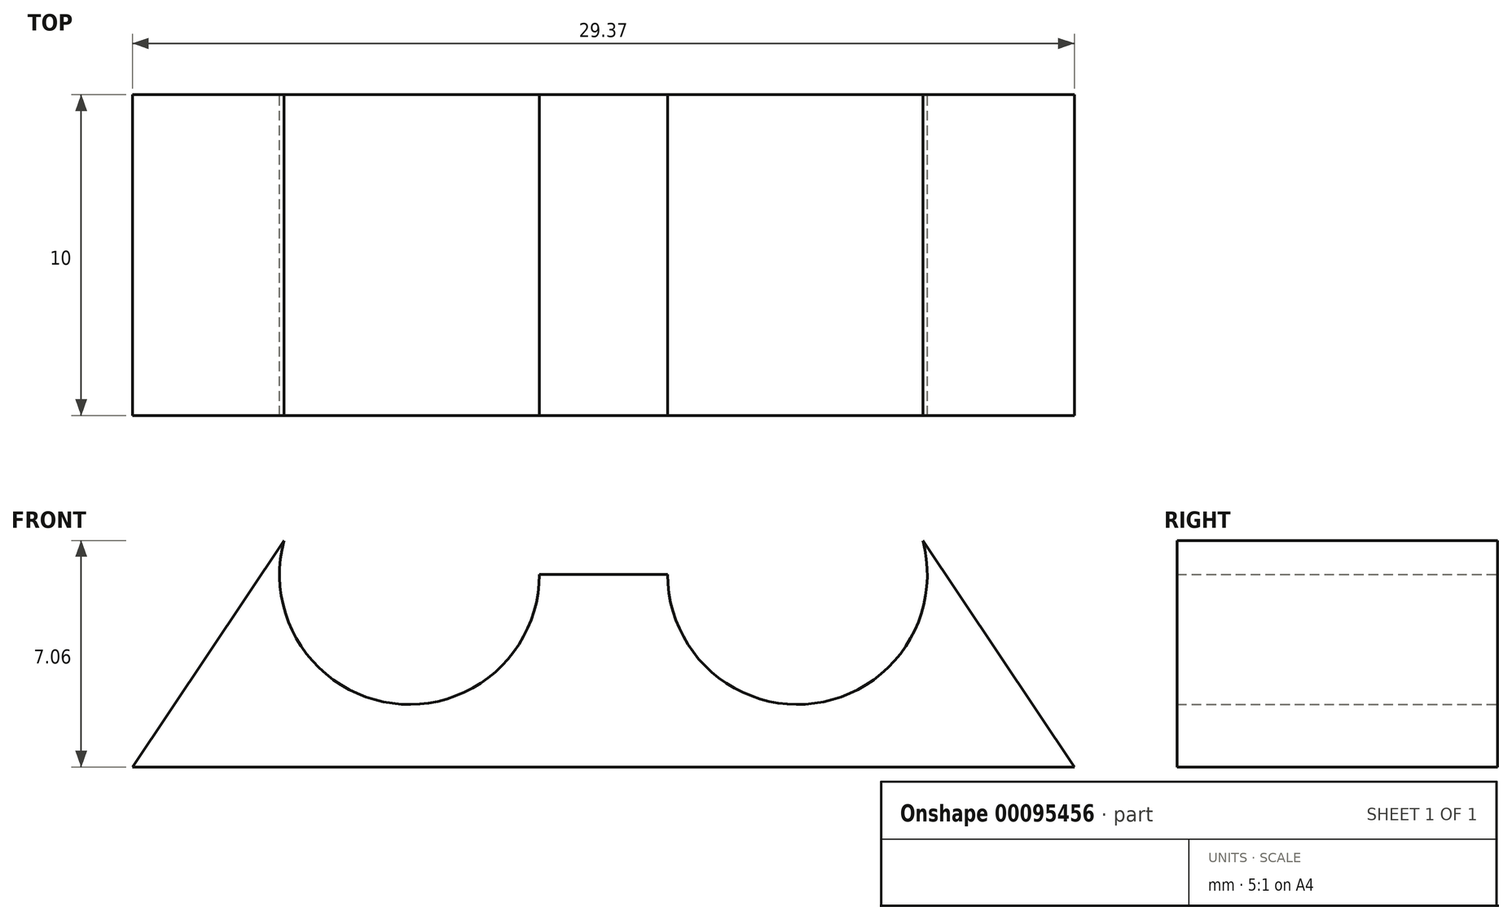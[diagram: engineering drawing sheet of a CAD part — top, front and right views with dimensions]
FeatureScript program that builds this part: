
annotation { "Feature Type Name" : "Feature", "Feature Type Description" : "" }
export const myFeature = defineFeature(function(context is Context, id is Id, definition is map)
    precondition{}
    {
        {
            var Q0;
            Q0=qCreatedBy(makeId("Front.planeOp"),FACE);
            var sketch = newSketch(context, id + "F0", { "sketchPlane" : qUnion([Q0])});
            skArc(sketch, "E0", {"start": v(-27.77, 1.06) * mm, "mid": v(-24.4, -4.01) * mm, "end": v(-19.81, 0) * mm});
            skLineSegment(sketch, "E1", {"start": v(0, 0) * mm, "end": v(-102.74, 0) * mm, "construction": true});
            skLineSegment(sketch, "E2", {"start": v(-27.77, 1.06) * mm, "end": v(-32.5, -6) * mm});
            skLineSegment(sketch, "E3", {"start": v(-32.5, -6) * mm, "end": v(-17.81, -6) * mm});
            skLineSegment(sketch, "E4", {"start": v(-19.81, 0) * mm, "end": v(-17.81, 0) * mm});
            skLineSegment(sketch, "E5", {"start": v(-17.81, 0) * mm, "end": v(-17.81, -6) * mm});
            skLineSegment(sketch, "E6.MirrorCS", {"start": v(-15.81, 0) * mm, "end": v(-17.81, 0) * mm});
            skArc(sketch, "E7.MirrorCS", {"start": v(-7.85, 1.06) * mm, "mid": v(-11.23, -4.01) * mm, "end": v(-15.81, 0) * mm});
            skLineSegment(sketch, "E8.MirrorCS", {"start": v(-7.85, 1.06) * mm, "end": v(-3.13, -6) * mm});
            skLineSegment(sketch, "E9.MirrorCS", {"start": v(-3.13, -6) * mm, "end": v(-17.81, -6) * mm});
            skSolve(sketch);
        }
        {
            var Q0;
            Q0 = qSketchRegion(id + "F0", true);
            extrude(context, id + "F1", {"entities" : qUnion([Q0]), "depth" : 10 * mm});
        }
    });
